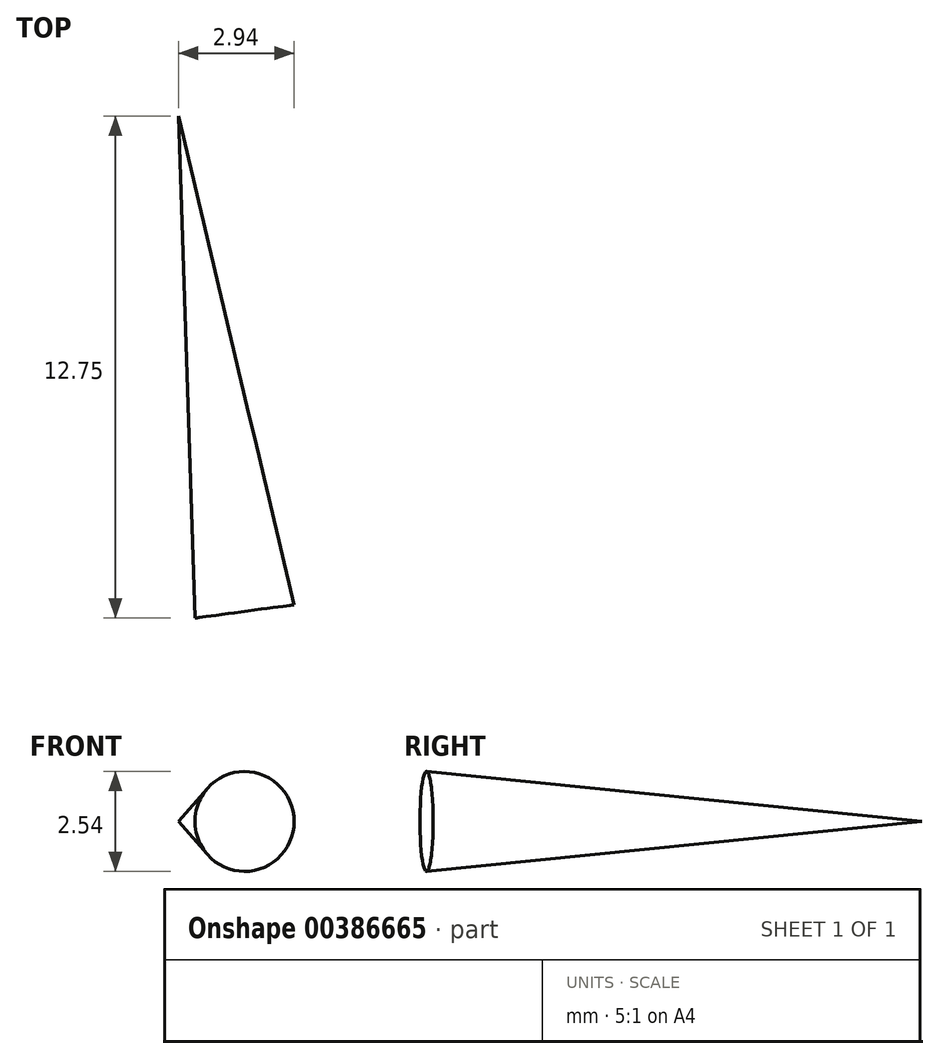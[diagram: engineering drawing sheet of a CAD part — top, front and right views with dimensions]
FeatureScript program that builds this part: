
annotation { "Feature Type Name" : "Feature", "Feature Type Description" : "" }
export const myFeature = defineFeature(function(context is Context, id is Id, definition is map)
    precondition{}
    {
        {
            var Q0;
            Q0=qCreatedBy(makeId("Top.planeOp"),FACE);
            var sketch = newSketch(context, id + "F0", { "sketchPlane" : qUnion([Q0])});
            skLineSegment(sketch, "E0", {"start": v(-17.19, -4.55) * mm, "end": v(-15.5, -17.13) * mm, "construction": true});
            skLineSegment(sketch, "E1", {"start": v(-15.5, -17.13) * mm, "end": v(-14.25, -16.97) * mm});
            skLineSegment(sketch, "E2", {"start": v(-17.19, -4.55) * mm, "end": v(-14.25, -16.97) * mm});
            skSolve(sketch);
        }
        {
            var Q0;
            Q0=sQuery(id+"F0.wireOp",EDGE,"E1");
            var Q1;
            Q1=sQuery(id+"F0.wireOp",EDGE,"E2");
            var Q2;
            Q2=sQuery(id+"F0.wireOp",EDGE,"E0");
            revolve(context, id + "F1", {"bodyType" : ToolBodyType.SURFACE, "surfaceEntities" : qUnion([Q0, Q1]), "axis" : qUnion([Q2]), "revolveType" : RevolveType.FULL});
        }
    });
